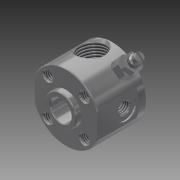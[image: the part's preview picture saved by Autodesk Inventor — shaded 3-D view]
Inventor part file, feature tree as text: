
AUTODESK INVENTOR PART (.ipt)
format: ipt  version: 2016 SP1 (Build 200210100, 210)  size: 293,376 bytes
history: native  units: in
note: dims shown in document units (in); Inventor stores cm internally (conversion verified against a paired STEP export)
features: other x42, sketch x14, revolve x5, extrude x5, hole x4, thread x4
ambient origin geometry x8: Origin, YZ Plane, XZ Plane, XY Plane, X Axis, Y Axis, Z Axis, Center Point
bodies: Solid1 (feature_tree)
feature tree (74):
  revolve  "Revolution1"  [1 undecoded]
  hole  "Hole1"  [1 undecoded]
  hole  "Hole2"  [1 undecoded]
  hole  "Hole3"  [1 undecoded]
  hole  "Hole4"  [1 undecoded]
  extrude  "Extrusion1"  Depth=0.252in TaperAngle=0.0deg
  revolve  "Revolution2"  [1 undecoded]
  thread  "Thread1"  [1 undecoded]
  revolve  "Revolution3"  [1 undecoded]
  thread  "Thread2"  [1 undecoded]
  extrude  "Extrusion2"  [1 undecoded]
  extrude  "Extrusion3"  [1 undecoded]
  extrude  "Extrusion4"  [1 undecoded]
  revolve  "Revolution4"  [1 undecoded]
  thread  "Thread3"  [1 undecoded]
  extrude  "Extrusion5"  [1 undecoded]
  revolve  "Revolution5"  [1 undecoded]
  thread  "Thread4"  [1 undecoded]
  other  "conn_XY"
  other  "conn_YZ"
  other  "conn_ZX"
  other  "conn_X"
  other  "conn_Y"
  other  "conn_Z"
  other  "conn_Center"
  other  "conn2_XY"
  other  "conn2_YZ"
  other  "conn2_ZX"
  other  "conn2_X"
  other  "conn2_Y"
  other  "conn2_Z"
  other  "conn2_Center"
  other  "mnt_XY"
  other  "mnt_YZ"
  other  "mnt_ZX"
  other  "mnt_X"
  other  "mnt_Y"
  other  "mnt_Z"
  other  "mnt_Center"
  other  "rod_XY"
  other  "rod_YZ"
  other  "rod_ZX"
  other  "rod_X"
  other  "rod_Y"
  other  "rod_Z"
  other  "rod_Center"
  other  "trun1_XY"
  other  "trun1_YZ"
  other  "trun1_ZX"
  other  "trun1_X"
  other  "trun1_Y"
  other  "trun1_Z"
  other  "trun1_Center"
  other  "trun2_XY"
  other  "trun2_YZ"
  other  "trun2_ZX"
  other  "trun2_X"
  other  "trun2_Y"
  other  "trun2_Z"
  other  "trun2_Center"
  sketch  "Sketch_3"  dims[d1=0.134in d2=0.28in d3=0.164in d4=0.25in d5=90.0deg d6=0.28in d7=0.8383in]
  sketch  "Sketch2"  dims[d0=360.0deg]
  sketch  "Sketch3"  dims[d8=0.134in d9=0.28in d10=0.164in d11=0.25in d12=90.0deg d13=0.28in d14=0.8383in]
  sketch  "Sketch4"  dims[d15=0.134in d16=0.28in d17=0.164in d18=0.25in d19=90.0deg d20=0.28in d21=0.8383in]
  sketch  "Sketch5"  dims[d22=0.134in d23=0.28in d24=0.164in d25=0.25in d26=90.0deg d27=0.28in d28=0.8383in d29=0.5915in d30=0.0in]
  sketch  "Sketch_6"  dims[d31=360.0deg d32=0.1399in d33=0.0in]
  sketch  "Sketch_7"  dims[d34=360.0deg d35=0.1399in d36=0.0in]
  sketch  "Sketch_8"  dims[d37=0.138in d38=0.0in d39=0.138in d40=0.0in]
  sketch  "Sketch_13"
  sketch  "Sketch_14"
  sketch  "Sketch_15"
  sketch  "Sketch_9"  dims[d41=0.094in d42=0.0in d43=360.0deg]
  sketch  "Sketch_11"  dims[d48=360.0deg d49=0.2731in d50=0.0in d51=0.0in d52=0.0in d53=0.0in d54=0.0in]
  sketch  "Sketch_10"  dims[d44=0.0573in d45=0.0in d46=0.252in d47=0.0in]
note: 17 required parameter values undecoded (feature->parameter linkage not recoverable at this tier; creation-order binding heuristic only, values carry confidence <= 0.55)